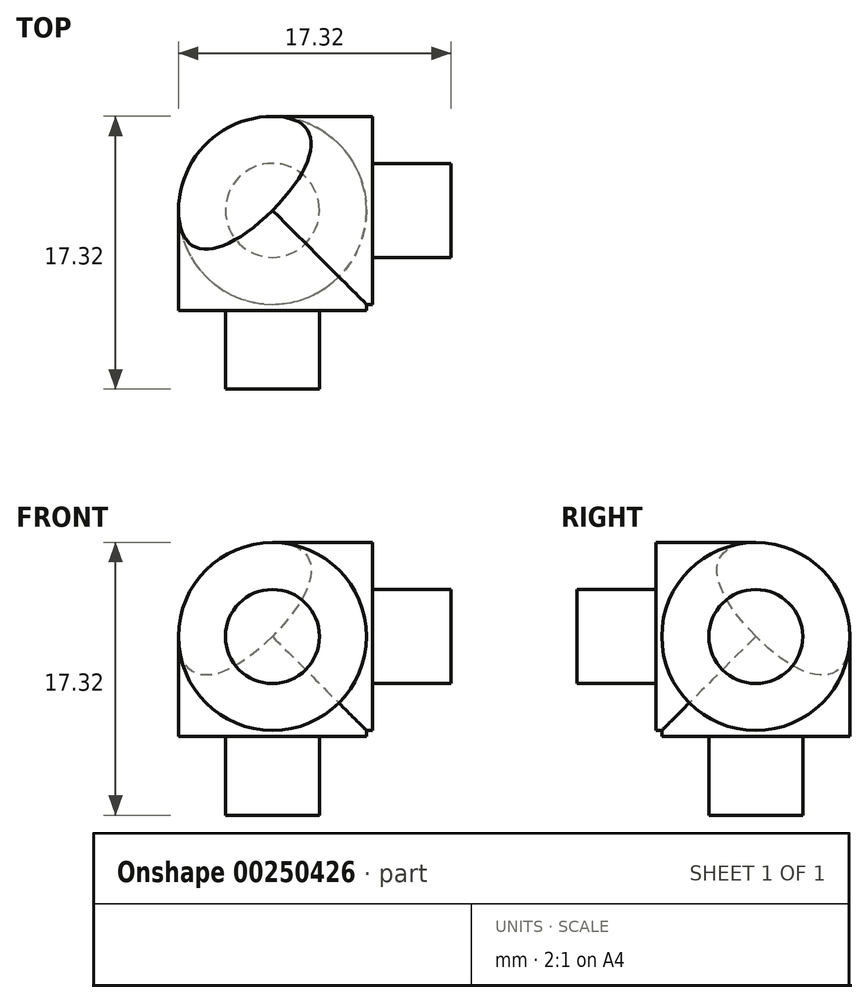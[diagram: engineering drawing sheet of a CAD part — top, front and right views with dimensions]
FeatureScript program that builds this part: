
annotation { "Feature Type Name" : "Feature", "Feature Type Description" : "" }
export const myFeature = defineFeature(function(context is Context, id is Id, definition is map)
    precondition{}
    {
        {
            var Q0;
            Q0=qCreatedBy(makeId("Top.planeOp"),FACE);
            var sketch = newSketch(context, id + "F0", { "sketchPlane" : qUnion([Q0])});
            skArc(sketch, "E0", {"start": v(0, 5.97) * mm, "mid": v(-4.22, 4.22) * mm, "end": v(-5.97, 0) * mm});
            skLineSegment(sketch, "E1", {"start": v(-5.97, 0) * mm, "end": v(-5.97, -6.35) * mm});
            skLineSegment(sketch, "E2", {"start": v(0, -6.35) * mm, "end": v(0, 0) * mm});
            skLineSegment(sketch, "E3", {"start": v(0, 0) * mm, "end": v(0, 5.97) * mm});
            skLineSegment(sketch, "E4", {"start": v(0, 0) * mm, "end": v(0, 0) * mm});
            skLineSegment(sketch, "E5", {"start": v(-2.98, -6.35) * mm, "end": v(-2.98, -11.35) * mm});
            skLineSegment(sketch, "E6", {"start": v(-2.98, -11.35) * mm, "end": v(0, -11.35) * mm});
            skLineSegment(sketch, "E7", {"start": v(0, -11.35) * mm, "end": v(0, -6.35) * mm});
            skLineSegment(sketch, "E8", {"start": v(-2.98, -6.35) * mm, "end": v(-5.97, -6.35) * mm});
            skSolve(sketch);
        }
        {
            var Q0;
            Q0 = qSketchRegion(id + "F0", true);
            var Q1;
            Q1=sQuery(id+"F0.wireOp",EDGE,"E3");
            revolve(context, id + "F1", {"entities" : qUnion([Q0]), "axis" : qUnion([Q1]), "revolveType" : RevolveType.FULL});
        }
        {
            var Q0;
            Q0=qCreatedBy(makeId("Top.planeOp"),FACE);
            var sketch = newSketch(context, id + "F2", { "sketchPlane" : qUnion([Q0])});
            skLineSegment(sketch, "E9", {"start": v(-64.78, 0) * mm, "end": v(54.44, 0) * mm, "construction": true});
            skSolve(sketch);
        }
        {
            var Q0;
            Q0=makeQuery(id+"F1.opRevolve","SWEPT_BODY",BODY,{"disambiguationData":[OSD([sQuery(id+"F0.wireOp",EDGE,"E0"),sQuery(id+"F0.wireOp",EDGE,"E1"),sQuery(id+"F0.wireOp",EDGE,"q7y0TzUk-fhFp-nIsZ-NEYz-1MwVzZ4vraMZ"),sQuery(id+"F0.wireOp",EDGE,"E2"),sQuery(id+"F0.wireOp",EDGE,"E3"),sQuery(id+"F0.wireOp",EDGE,"E4")])]});
            var Q1;
            Q1=sQuery(id+"F2.wireOp",EDGE,"E9");
            circularPattern(context, id + "F3", {"entities" : qUnion([Q0]), "axis" : qUnion([Q1]), "angle" : 90 * degree, "instanceCount" : 2, "equalSpace" : true});
        }
        {
            var Q0;
            Q0=qCreatedBy(makeId("Right.planeOp"),FACE);
            var sketch = newSketch(context, id + "F4", { "sketchPlane" : qUnion([Q0])});
            skLineSegment(sketch, "E10", {"start": v(0, -52.44) * mm, "end": v(0, 42.28) * mm});
            skSolve(sketch);
        }
        {
            var Q0;
            Q0=makeQuery(id+"F1.opRevolve","SWEPT_BODY",BODY,{"disambiguationData":[OSD([sQuery(id+"F0.wireOp",EDGE,"E0"),sQuery(id+"F0.wireOp",EDGE,"E1"),sQuery(id+"F0.wireOp",EDGE,"q7y0TzUk-fhFp-nIsZ-NEYz-1MwVzZ4vraMZ"),sQuery(id+"F0.wireOp",EDGE,"E2"),sQuery(id+"F0.wireOp",EDGE,"E3"),sQuery(id+"F0.wireOp",EDGE,"E4")])]});
            var Q1;
            Q1=sQuery(id+"F4.wireOp",EDGE,"E10");
            circularPattern(context, id + "F5", {"entities" : qUnion([Q0]), "axis" : qUnion([Q1]), "angle" : 90 * degree, "instanceCount" : 2, "equalSpace" : true});
        }
        {
            var Q0;
            Q0=makeQuery(id+"F1.opRevolve","SWEPT_BODY",BODY,{"disambiguationData":[OSD([sQuery(id+"F0.wireOp",EDGE,"E0"),sQuery(id+"F0.wireOp",EDGE,"E1"),sQuery(id+"F0.wireOp",EDGE,"q7y0TzUk-fhFp-nIsZ-NEYz-1MwVzZ4vraMZ"),sQuery(id+"F0.wireOp",EDGE,"E2"),sQuery(id+"F0.wireOp",EDGE,"E3"),sQuery(id+"F0.wireOp",EDGE,"E4")])]});
            var Q1;
            Q1=makeQuery(id+"F3.opPattern","COPY",BODY,{"derivedFrom":makeQuery(id+"F1.opRevolve","SWEPT_BODY",BODY,{"disambiguationData":[OSD([sQuery(id+"F0.wireOp",EDGE,"E0"),sQuery(id+"F0.wireOp",EDGE,"E1"),sQuery(id+"F0.wireOp",EDGE,"q7y0TzUk-fhFp-nIsZ-NEYz-1MwVzZ4vraMZ"),sQuery(id+"F0.wireOp",EDGE,"E2"),sQuery(id+"F0.wireOp",EDGE,"E3"),sQuery(id+"F0.wireOp",EDGE,"E4")])]}),"instanceName":"1"});
            var Q2;
            Q2=makeQuery(id+"F5.opPattern","COPY",BODY,{"derivedFrom":makeQuery(id+"F1.opRevolve","SWEPT_BODY",BODY,{"disambiguationData":[OSD([sQuery(id+"F0.wireOp",EDGE,"E0"),sQuery(id+"F0.wireOp",EDGE,"E1"),sQuery(id+"F0.wireOp",EDGE,"q7y0TzUk-fhFp-nIsZ-NEYz-1MwVzZ4vraMZ"),sQuery(id+"F0.wireOp",EDGE,"E2"),sQuery(id+"F0.wireOp",EDGE,"E3"),sQuery(id+"F0.wireOp",EDGE,"E4")])]}),"instanceName":"1"});
            booleanBodies(context, id + "F6", {"operationType" : BooleanOperationType.UNION, "tools" : qUnion([Q0, Q1, Q2])});
        }
        {
            var Q0;
            {var subQ0=makeQuery(id+"F1.opRevolve","SWEPT_FACE",FACE,{"disambiguationData":[OSD([sQuery(id+"F0.wireOp",EDGE,"E1")])]});var subQ1=makeQuery(id+"F1.opRevolve","SWEPT_FACE",FACE,{"disambiguationData":[OSD([sQuery(id+"F0.wireOp",EDGE,"E0")])]});Q0=makeQuery(id+"F6.opBoolean","INTERSECT",VERTEX,{"derivedFrom":[subQ1,subQ0,makeQuery(id+"F3.opPattern","COPY",FACE,{"derivedFrom":subQ1,"instanceName":"1"}),makeQuery(id+"F5.opPattern","COPY",FACE,{"derivedFrom":subQ0,"instanceName":"1"})]});}
            var Q1;
            {var subQ0=makeQuery(id+"F1.opRevolve","SWEPT_FACE",FACE,{"disambiguationData":[OSD([sQuery(id+"F0.wireOp",EDGE,"E0")])]});var subQ1=makeQuery(id+"F1.opRevolve","SWEPT_FACE",FACE,{"disambiguationData":[OSD([sQuery(id+"F0.wireOp",EDGE,"E1")])]});Q1=makeQuery(id+"F6.opBoolean","INTERSECT",VERTEX,{"derivedFrom":[subQ0,subQ1,makeQuery(id+"F3.opPattern","COPY",FACE,{"derivedFrom":subQ1,"instanceName":"1"}),makeQuery(id+"F5.opPattern","COPY",FACE,{"derivedFrom":subQ0,"instanceName":"1"})]});}
            var Q2;
            {var subQ0=makeQuery(id+"F1.opRevolve","SWEPT_FACE",FACE,{"disambiguationData":[OSD([sQuery(id+"F0.wireOp",EDGE,"E1")])]});var subQ1=makeQuery(id+"F1.opRevolve","SWEPT_FACE",FACE,{"disambiguationData":[OSD([sQuery(id+"F0.wireOp",EDGE,"E0")])]});Q2=makeQuery(id+"F6.opBoolean","INTERSECT",VERTEX,{"derivedFrom":[subQ1,makeQuery(id+"F3.opPattern","COPY",FACE,{"derivedFrom":subQ1,"instanceName":"1"}),makeQuery(id+"F3.opPattern","COPY",FACE,{"derivedFrom":subQ0,"instanceName":"1"}),makeQuery(id+"F5.opPattern","COPY",FACE,{"derivedFrom":subQ1,"instanceName":"1"}),makeQuery(id+"F5.opPattern","COPY",FACE,{"derivedFrom":subQ0,"instanceName":"1"})]});}
            cPlane(context, id + "F7", {"entities" : qUnion([Q0, Q1, Q2]), "cplaneType" : CPlaneType.THREE_POINT, "offset" : 25 * mm, "width" : 150 * mm, "height" : 150 * mm});
        }
        {
            var Q0;
            Q0=qCreatedBy(id+"F7.planeOp",FACE);
            var sketch = newSketch(context, id + "F8", { "sketchPlane" : qUnion([Q0])});
            skCircle(sketch, "E11", {"center": v(0, 0) * mm, "radius": 6.63 * mm});
            skPoint(sketch, "E12.0", {"position": v(6.63, 0) * mm});
            skSolve(sketch);
        }
        {
            var Q0;
            Q0 = qSketchRegion(id + "F8", true);
            extrude(context, id + "F9", {"entities" : qUnion([Q0]), "operationType" : NewBodyOperationType.REMOVE, "depth" : 25 * mm});
        }
    });
